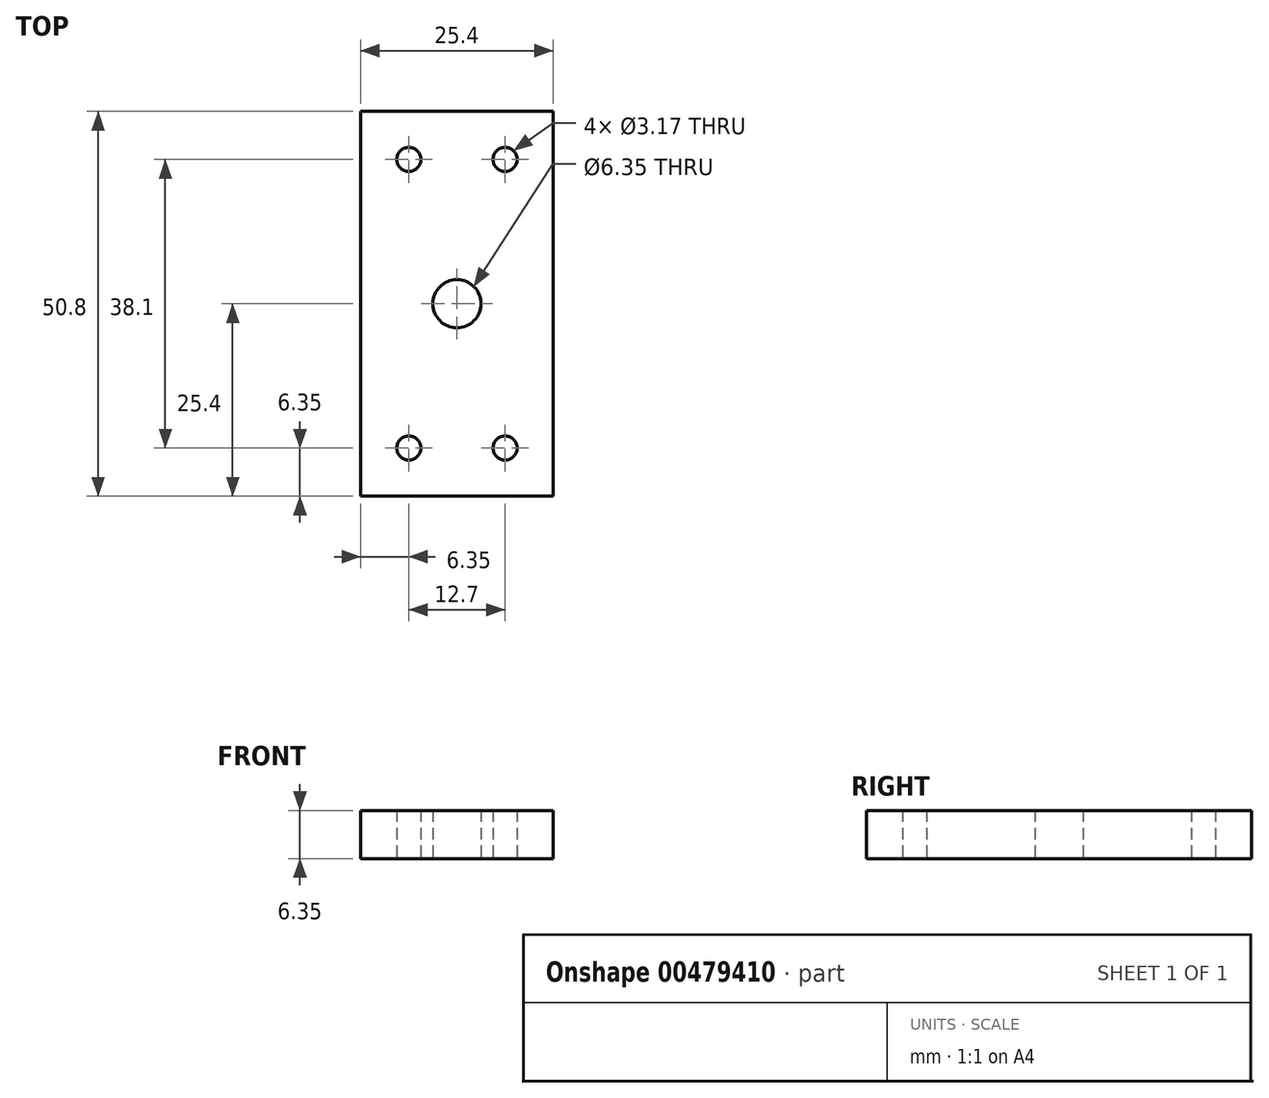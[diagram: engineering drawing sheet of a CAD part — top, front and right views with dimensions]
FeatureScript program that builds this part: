
annotation { "Feature Type Name" : "Feature", "Feature Type Description" : "" }
export const myFeature = defineFeature(function(context is Context, id is Id, definition is map)
    precondition{}
    {
        {
            var Q0;
            Q0=qCreatedBy(makeId("Top.planeOp"),FACE);
            var sketch = newSketch(context, id + "F0", { "sketchPlane" : qUnion([Q0]), "disableImprinting" : false});
            skLineSegment(sketch, "E0.bottom", {"start": v(0, 0) * mm, "end": v(25.4, 0) * mm});
            skLineSegment(sketch, "E0.top", {"start": v(0, 50.8) * mm, "end": v(25.4, 50.8) * mm});
            skLineSegment(sketch, "E0.left", {"start": v(0, 0) * mm, "end": v(0, 50.8) * mm});
            skLineSegment(sketch, "E0.right", {"start": v(25.4, 0) * mm, "end": v(25.4, 50.8) * mm});
            skCircle(sketch, "E1", {"center": v(12.7, 25.4) * mm, "radius": 3.18 * mm});
            skCircle(sketch, "E2", {"center": v(6.35, 44.45) * mm, "radius": 1.59 * mm});
            skCircle(sketch, "E3", {"center": v(19.05, 44.45) * mm, "radius": 1.59 * mm});
            skCircle(sketch, "E4", {"center": v(6.35, 6.35) * mm, "radius": 1.59 * mm});
            skCircle(sketch, "E5", {"center": v(19.05, 6.35) * mm, "radius": 1.59 * mm});
            skSolve(sketch);
        }
        {
            var Q0;
            Q0=makeQuery(id+"F0.imprint","IMPRINT",FACE,{"disambiguationData":[TD([[makeQuery(id+"F0.imprint","IMPRINT",EDGE,{"derivedFrom":sQuery(id+"F0.wireOp",EDGE,"E0.bottom")}),1.0]])]});
            extrude(context, id + "F1", {"entities" : qUnion([Q0]), "depth" : 6.35 * mm, "offsetDistance" : 25.4 * mm});
        }
    });
